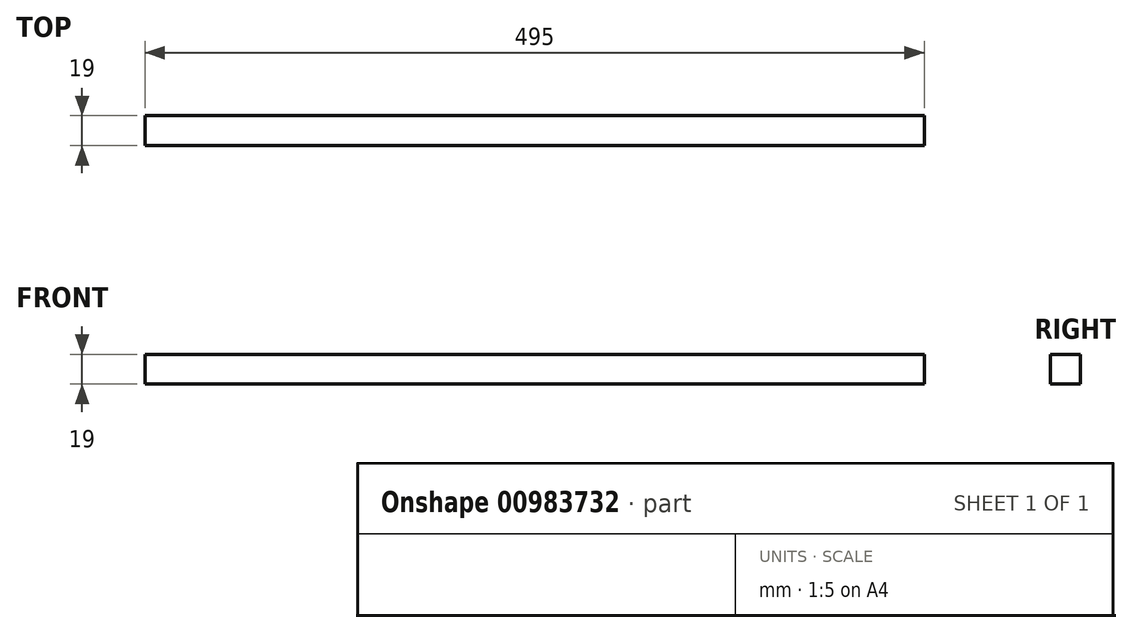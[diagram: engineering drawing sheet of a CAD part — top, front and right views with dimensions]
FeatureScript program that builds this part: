
annotation { "Feature Type Name" : "Feature", "Feature Type Description" : "" }
export const myFeature = defineFeature(function(context is Context, id is Id, definition is map)
    precondition{}
    {
        {
            var Q0;
            Q0=qCreatedBy(makeId("Front.planeOp"),FACE);
            var sketch = newSketch(context, id + "F0", { "sketchPlane" : qUnion([Q0])});
            skLineSegment(sketch, "E0.bottom", {"start": v(-50.7, 19) * mm, "end": v(444.3, 19) * mm});
            skLineSegment(sketch, "E0.top", {"start": v(-50.7, 0) * mm, "end": v(444.3, 0) * mm});
            skLineSegment(sketch, "E0.left", {"start": v(-50.7, 19) * mm, "end": v(-50.7, 0) * mm});
            skLineSegment(sketch, "E0.right", {"start": v(444.3, 19) * mm, "end": v(444.3, 0) * mm});
            skSolve(sketch);
        }
        {
            var Q0;
            Q0 = qSketchRegion(id + "F0", true);
            extrude(context, id + "F1", {"entities" : qUnion([Q0]), "depth" : 19 * mm, "offsetDistance" : 25.4 * mm});
        }
    });
